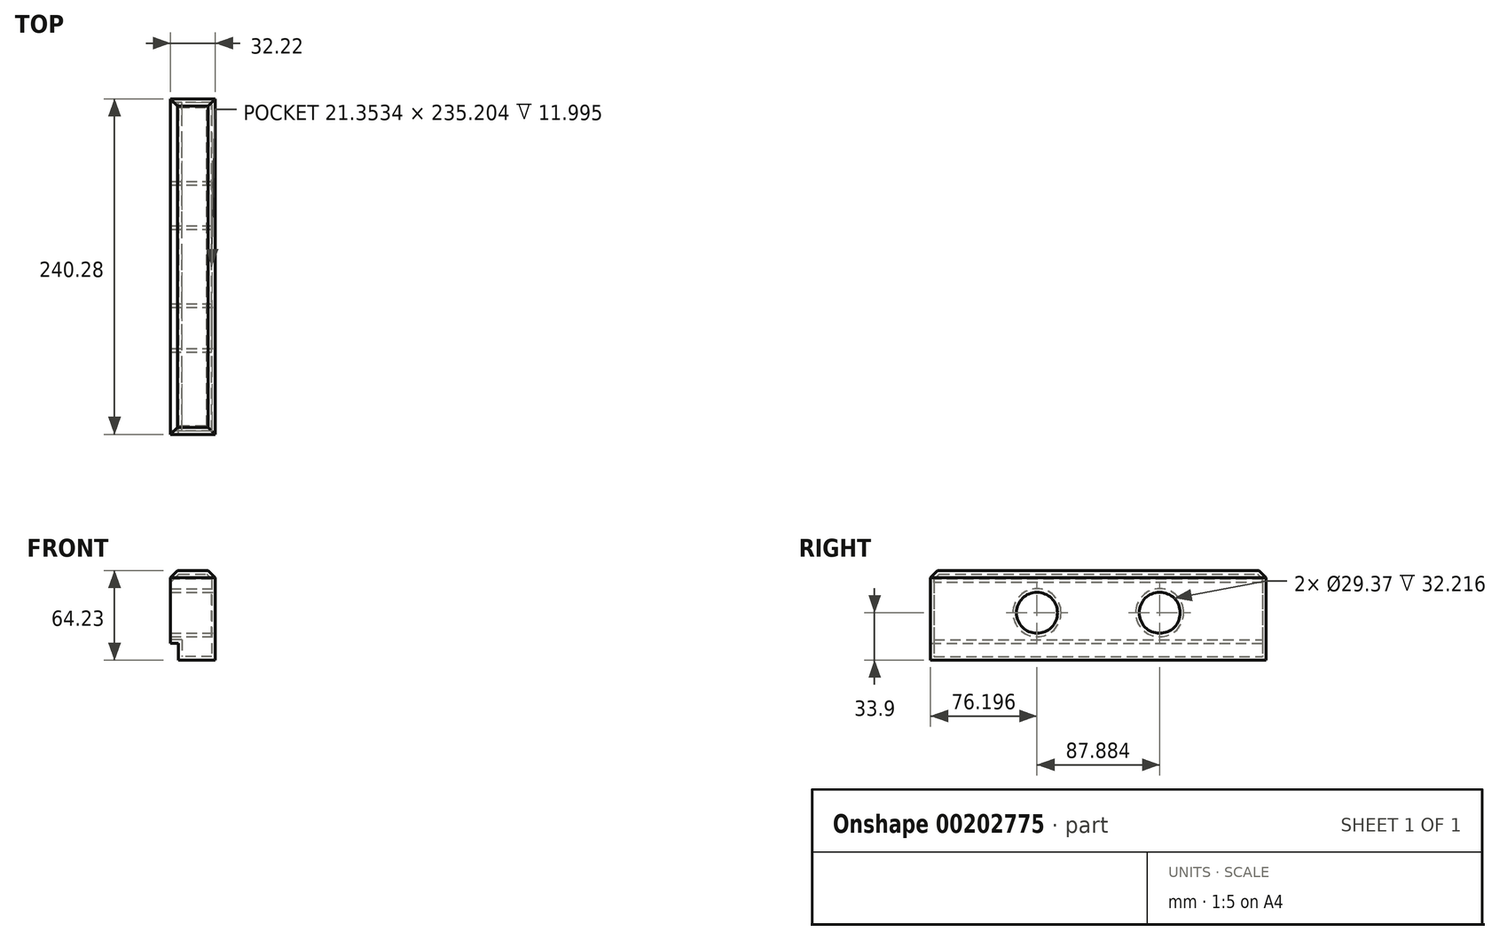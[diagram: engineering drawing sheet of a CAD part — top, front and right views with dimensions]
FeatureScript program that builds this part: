
annotation { "Feature Type Name" : "Feature", "Feature Type Description" : "" }
export const myFeature = defineFeature(function(context is Context, id is Id, definition is map)
    precondition{}
    {
        {
            var Q0;
            Q0=qCreatedBy(makeId("Front.planeOp"),FACE);
            var sketch = newSketch(context, id + "F0", { "sketchPlane" : qUnion([Q0])});
            skLineSegment(sketch, "E0.bottom", {"start": v(-47.08, 75.83) * mm, "end": v(-79.3, 75.83) * mm});
            skLineSegment(sketch, "E0.top", {"start": v(-47.08, 11.6) * mm, "end": v(-79.3, 11.6) * mm});
            skLineSegment(sketch, "E0.left", {"start": v(-47.08, 75.83) * mm, "end": v(-47.08, 11.6) * mm});
            skLineSegment(sketch, "E0.right", {"start": v(-79.3, 75.83) * mm, "end": v(-79.3, 11.6) * mm});
            skLineSegment(sketch, "E1.bottom", {"start": v(-73.52, 23.6) * mm, "end": v(-79.3, 23.6) * mm});
            skLineSegment(sketch, "E1.top", {"start": v(-73.52, 11.6) * mm, "end": v(-79.3, 11.6) * mm});
            skLineSegment(sketch, "E1.left", {"start": v(-73.52, 23.6) * mm, "end": v(-73.52, 11.6) * mm});
            skLineSegment(sketch, "E1.right", {"start": v(-79.3, 23.6) * mm, "end": v(-79.3, 11.6) * mm});
            skSolve(sketch);
        }
        {
            var Q0;
            Q0=makeQuery(id+"F0.imprint","IMPRINT",FACE,{"disambiguationData":[TD([[makeQuery(id+"F0.imprint","IMPRINT",EDGE,{"derivedFrom":sQuery(id+"F0.wireOp",EDGE,"E0.bottom")}),1.0]])]});
            extrude(context, id + "F1", {"entities" : qUnion([Q0]), "depth" : 240.28 * mm});
        }
        {
            var Q0;
            Q0=makeQuery(id+"F1.opExtrude","SWEPT_FACE",FACE,{"disambiguationData":[OSD([sQuery(id+"F0.wireOp",EDGE,"E0.left")])]});
            var sketch = newSketch(context, id + "F2", { "sketchPlane" : qUnion([Q0])});
            skCircle(sketch, "E2", {"center": v(-76.2, 45.5) * mm, "radius": 14.68 * mm});
            skLineSegment(sketch, "E3", {"start": v(-120.14, 75.83) * mm, "end": v(-120.14, 11.6) * mm, "construction": true});
            skCircle(sketch, "E4.MirrorC", {"center": v(-164.08, 45.5) * mm, "radius": 14.68 * mm});
            skSolve(sketch);
        }
        {
            var Q0;
            Q0 = qSketchRegion(id + "F2", true);
            extrude(context, id + "F3", {"entities" : qUnion([Q0]), "operationType" : NewBodyOperationType.REMOVE, "endBound" : BoundingType.THROUGH_ALL, "oppositeDirection" : true, "depth" : 25.4 * mm});
        }
        {
            var Q0;
            Q0=makeQuery(id+"F1.opExtrude","SWEPT_EDGE",EDGE,{"disambiguationData":[OSD([sQuery(id+"F0.wireOp",EDGE,"E0.bottom"),sQuery(id+"F0.wireOp",EDGE,"E0.right")])]});
            var Q1;
            Q1=makeQuery(id+"F1.opExtrude","CAP_EDGE",EDGE,{"disambiguationData":[OSD([sQuery(id+"F0.wireOp",EDGE,"E0.bottom")])],"isStart":true});
            var Q2;
            Q2=makeQuery(id+"F1.opExtrude","SWEPT_EDGE",EDGE,{"disambiguationData":[OSD([sQuery(id+"F0.wireOp",EDGE,"E0.bottom"),sQuery(id+"F0.wireOp",EDGE,"E0.left")])]});
            var Q3;
            Q3=makeQuery(id+"F1.opExtrude","CAP_EDGE",EDGE,{"disambiguationData":[OSD([sQuery(id+"F0.wireOp",EDGE,"E0.bottom")])],"isStart":false});
            chamfer(context, id + "F4", {"entities" : qUnion([Q0, Q1, Q2, Q3]), "width" : 5.08 * mm, "tangentPropagation" : true});
        }
        {
            var Q0;
            Q0=makeQuery(id+"F1.opExtrude","SWEPT_FACE",FACE,{"disambiguationData":[OSD([sQuery(id+"F0.wireOp",EDGE,"E0.right")])]});
            shell(context, id + "F5", {"entities" : qUnion([Q0]), "thickness" : 2.54 * mm});
        }
    });
